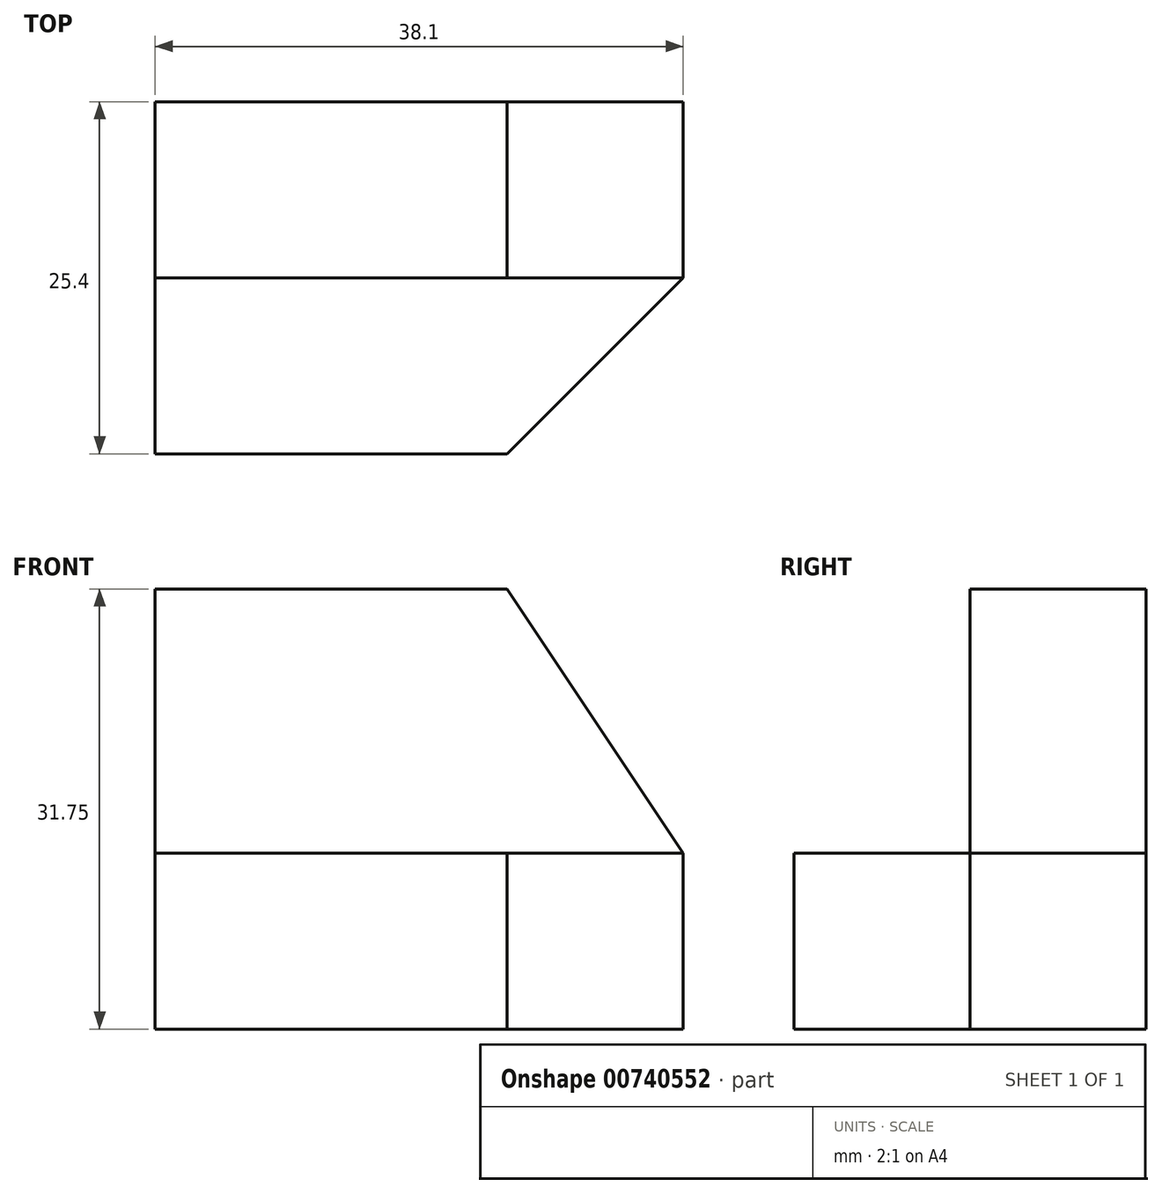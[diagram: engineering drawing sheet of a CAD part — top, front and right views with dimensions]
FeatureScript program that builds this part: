
annotation { "Feature Type Name" : "Feature", "Feature Type Description" : "" }
export const myFeature = defineFeature(function(context is Context, id is Id, definition is map)
    precondition{}
    {
        {
            var Q0;
            Q0=qCreatedBy(makeId("Front.planeOp"),FACE);
            var sketch = newSketch(context, id + "F0", { "sketchPlane" : qUnion([Q0])});
            skLineSegment(sketch, "E0", {"start": v(0, 0) * mm, "end": v(0, 31.75) * mm});
            skLineSegment(sketch, "E1", {"start": v(0, 31.75) * mm, "end": v(38.1, 31.75) * mm});
            skLineSegment(sketch, "E2", {"start": v(38.1, 31.75) * mm, "end": v(38.1, 0) * mm});
            skLineSegment(sketch, "E3", {"start": v(38.1, 0) * mm, "end": v(0, 0) * mm});
            skSolve(sketch);
        }
        {
            var Q0;
            Q0 = qSketchRegion(id + "F0", true);
            extrude(context, id + "F1", {"entities" : qUnion([Q0]), "depth" : 25.4 * mm, "offsetDistance" : 25.4 * mm});
        }
        {
            var Q0;
            Q0=makeQuery(id+"F1.opExtrude","SWEPT_FACE",FACE,{"disambiguationData":[OSD([sQuery(id+"F0.wireOp",EDGE,"E2")])]});
            var sketch = newSketch(context, id + "F2", { "sketchPlane" : qUnion([Q0])});
            skLineSegment(sketch, "E4", {"start": v(-12.7, 31.75) * mm, "end": v(-12.7, 12.7) * mm});
            skLineSegment(sketch, "E5", {"start": v(-12.7, 12.7) * mm, "end": v(-25.4, 12.7) * mm});
            skSolve(sketch);
        }
        {
            var Q0;
            {var subQ0=sQuery(id+"F2.wireOp",EDGE,"E4");Q0=makeQuery(id+"F2.imprint","IMPRINT",FACE,{"disambiguationData":[TD([[makeQuery(id+"F2.imprint","IMPRINT",EDGE,{"derivedFrom":subQ0}),-1.0]])]});}
            extrude(context, id + "F3", {"entities" : qUnion([Q0]), "operationType" : NewBodyOperationType.REMOVE, "endBound" : BoundingType.THROUGH_ALL, "oppositeDirection" : true, "depth" : 25.4 * mm, "offsetDistance" : 25.4 * mm});
        }
        {
            var Q0;
            Q0=makeQuery(id+"F3.boolean.opBoolean","COPY",FACE,{"derivedFrom":makeQuery(id+"F3.opExtrude","SWEPT_FACE",FACE,{"disambiguationData":[OSD([sQuery(id+"F2.wireOp",EDGE,"E4")])]})});
            var sketch = newSketch(context, id + "F4", { "sketchPlane" : qUnion([Q0])});
            skLineSegment(sketch, "E6", {"start": v(25.4, 31.75) * mm, "end": v(38.1, 12.7) * mm});
            skSolve(sketch);
        }
        {
            var Q0;
            Q0 = qSketchRegion(id + "F4", true);
            var Q1;
            {var subQ0=sQuery(id+"F4.wireOp",EDGE,"E6");Q1=makeQuery(id+"F4.imprint","IMPRINT",FACE,{"disambiguationData":[TD([[makeQuery(id+"F4.imprint","IMPRINT",EDGE,{"derivedFrom":subQ0}),1.0]])]});}
            extrude(context, id + "F5", {"entities" : qUnion([Q0, Q1]), "operationType" : NewBodyOperationType.REMOVE, "endBound" : BoundingType.THROUGH_ALL, "oppositeDirection" : true, "depth" : 25.4 * mm, "offsetDistance" : 25.4 * mm});
        }
        {
            var Q0;
            Q0=makeQuery(id+"F3.boolean.opBoolean","COPY",FACE,{"derivedFrom":makeQuery(id+"F3.opExtrude","SWEPT_FACE",FACE,{"disambiguationData":[OSD([sQuery(id+"F2.wireOp",EDGE,"E5")])]})});
            var sketch = newSketch(context, id + "F6", { "sketchPlane" : qUnion([Q0])});
            skLineSegment(sketch, "E7", {"start": v(38.1, -12.7) * mm, "end": v(25.4, -25.4) * mm});
            skSolve(sketch);
        }
        {
            var Q0;
            Q0 = qSketchRegion(id + "F6", true);
            var Q1;
            {var subQ0=sQuery(id+"F6.wireOp",EDGE,"E7");Q1=makeQuery(id+"F6.imprint","IMPRINT",FACE,{"disambiguationData":[TD([[makeQuery(id+"F6.imprint","IMPRINT",EDGE,{"derivedFrom":subQ0}),1.0]])]});}
            extrude(context, id + "F7", {"entities" : qUnion([Q0, Q1]), "operationType" : NewBodyOperationType.REMOVE, "endBound" : BoundingType.THROUGH_ALL, "oppositeDirection" : true, "depth" : 25.4 * mm, "offsetDistance" : 25.4 * mm});
        }
    });
